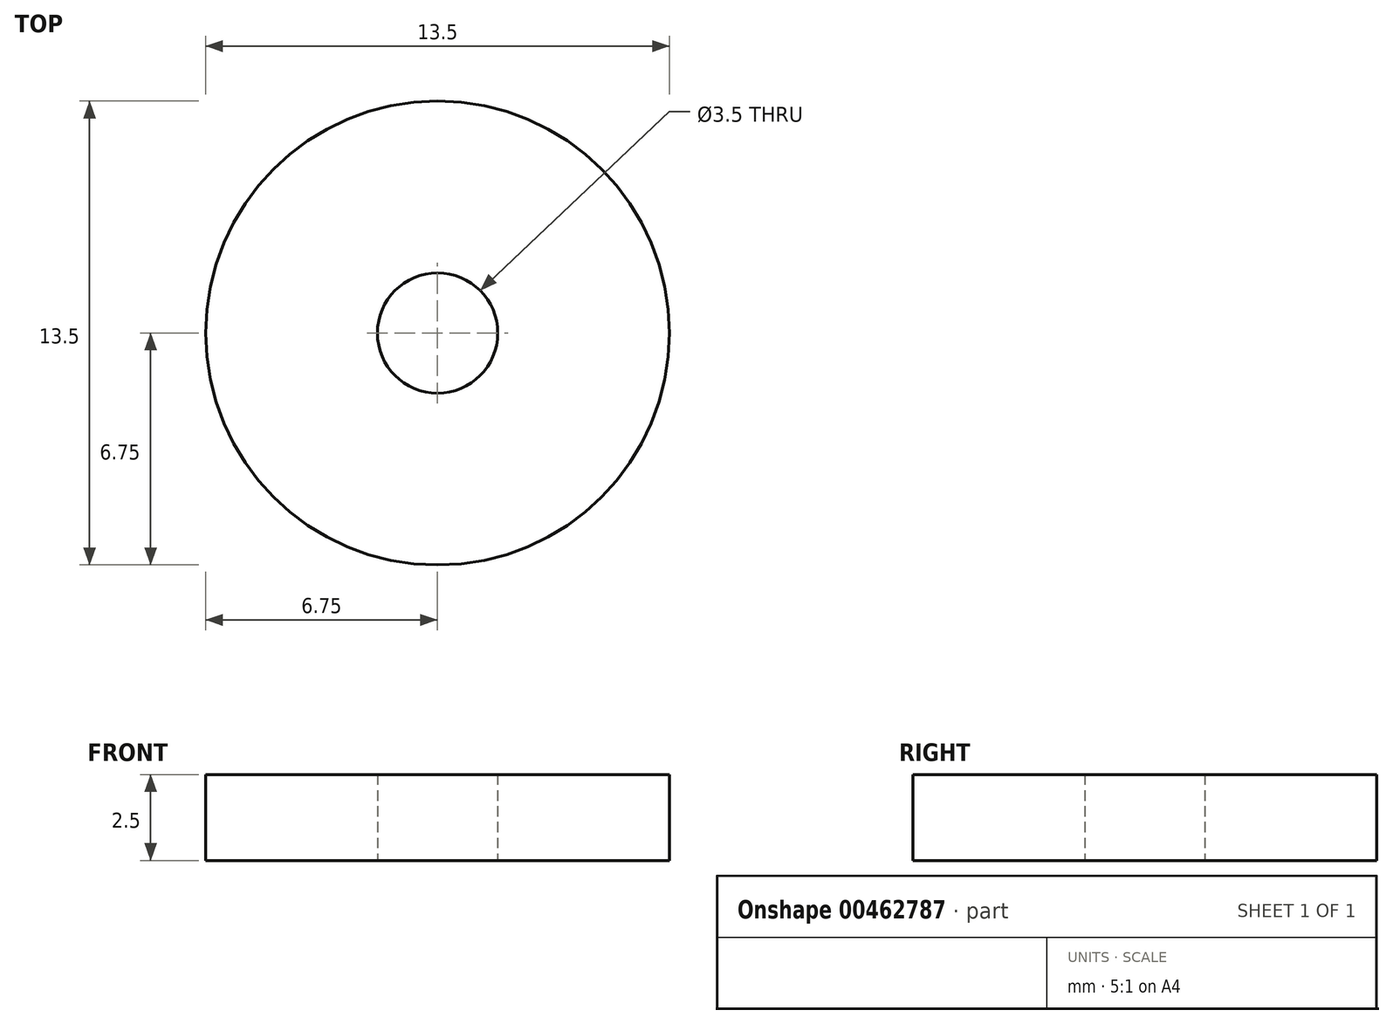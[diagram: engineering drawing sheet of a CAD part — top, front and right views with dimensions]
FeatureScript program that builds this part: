
annotation { "Feature Type Name" : "Feature", "Feature Type Description" : "" }
export const myFeature = defineFeature(function(context is Context, id is Id, definition is map)
    precondition{}
    {
        {
            var Q0;
            Q0=qCreatedBy(makeId("Top.planeOp"),FACE);
            var sketch = newSketch(context, id + "F0", { "sketchPlane" : qUnion([Q0])});
            skCircle(sketch, "E0", {"center": v(0, 0) * mm, "radius": 1.75 * mm});
            skCircle(sketch, "E1", {"center": v(0, 0) * mm, "radius": 6.75 * mm});
            skSolve(sketch);
        }
        {
            var Q0;
            Q0=makeQuery(id+"F0.imprint","IMPRINT",FACE,{"disambiguationData":[TD([[makeQuery(id+"F0.imprint","IMPRINT",EDGE,{"derivedFrom":sQuery(id+"F0.wireOp",EDGE,"E0")}),-1.0]])]});
            extrude(context, id + "F1", {"entities" : qUnion([Q0]), "depth" : 2.5 * mm});
        }
    });
